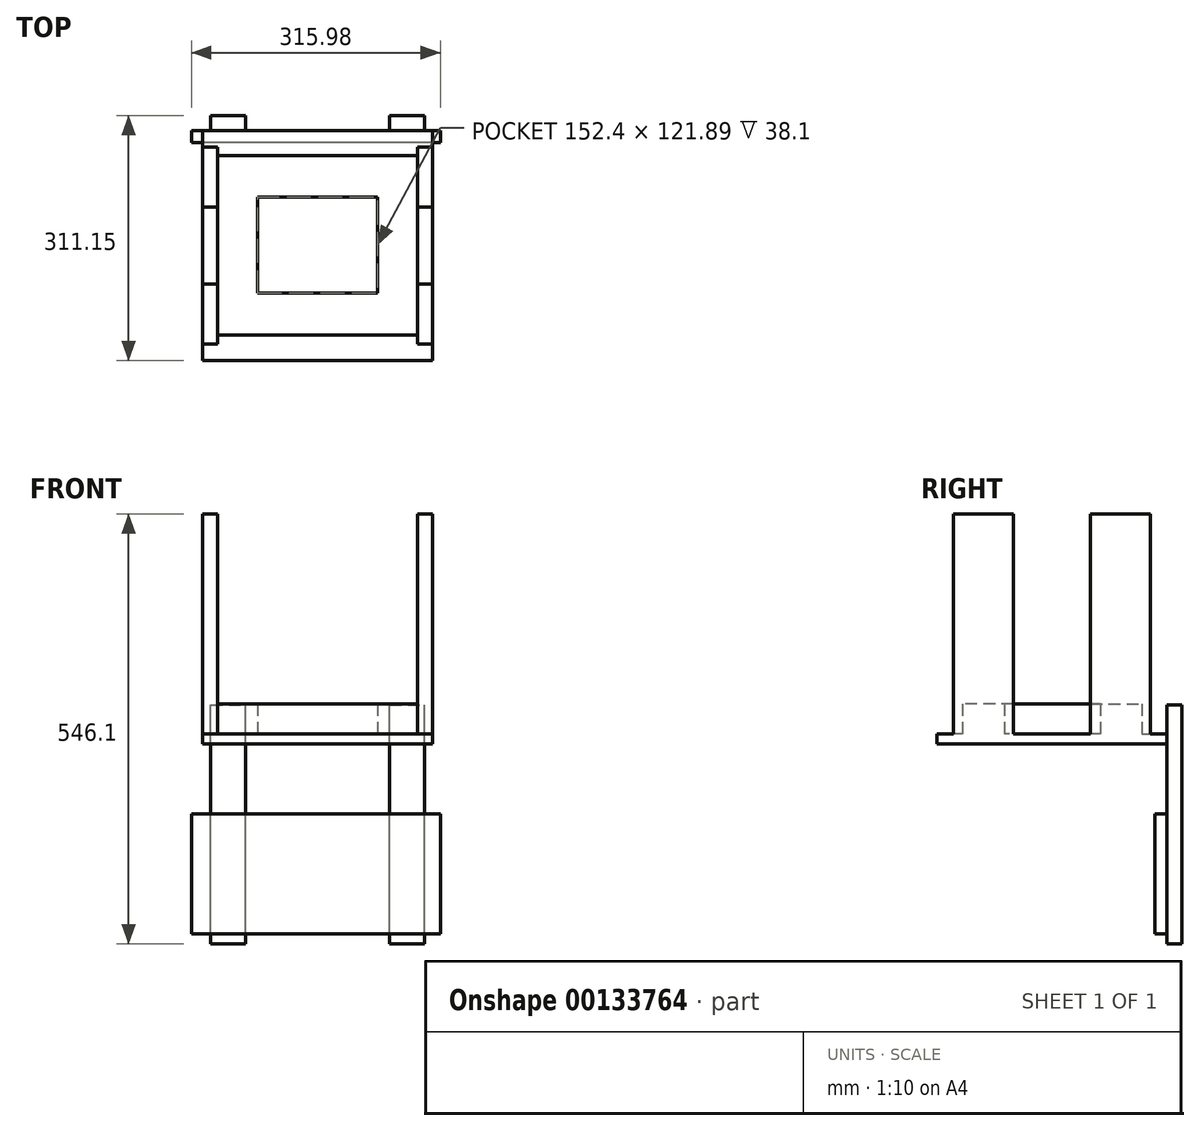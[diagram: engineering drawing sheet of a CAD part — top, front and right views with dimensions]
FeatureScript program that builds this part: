
annotation { "Feature Type Name" : "Feature", "Feature Type Description" : "" }
export const myFeature = defineFeature(function(context is Context, id is Id, definition is map)
    precondition{}
    {
        {
            var Q0;
            Q0=qCreatedBy(makeId("Top.planeOp"),FACE);
            var sketch = newSketch(context, id + "F0", { "sketchPlane" : qUnion([Q0])});
            skLineSegment(sketch, "E0.bottom", {"start": v(-155.55, 178.7) * mm, "end": v(136.55, 178.7) * mm});
            skLineSegment(sketch, "E0.top", {"start": v(-155.55, -113.4) * mm, "end": v(136.55, -113.4) * mm});
            skLineSegment(sketch, "E0.left", {"start": v(-155.55, 178.7) * mm, "end": v(-155.55, -113.4) * mm});
            skLineSegment(sketch, "E0.right", {"start": v(136.55, 178.7) * mm, "end": v(136.55, -113.4) * mm});
            skSolve(sketch);
        }
        {
            var Q0;
            Q0=makeQuery(id+"F0.imprint","IMPRINT",FACE,{"disambiguationData":[TD([[makeQuery(id+"F0.imprint","IMPRINT",EDGE,{"derivedFrom":sQuery(id+"F0.wireOp",EDGE,"E0.bottom")}),-1.0]])]});
            extrude(context, id + "F1", {"entities" : qUnion([Q0]), "oppositeDirection" : true, "depth" : 12.7 * mm});
        }
        {
            var Q0;
            Q0=makeQuery(id+"F1.opExtrude","CAP_FACE",FACE,{"disambiguationData":[OSD([sQuery(id+"F0.wireOp",EDGE,"E0.bottom"),sQuery(id+"F0.wireOp",EDGE,"E0.top"),sQuery(id+"F0.wireOp",EDGE,"E0.left"),sQuery(id+"F0.wireOp",EDGE,"E0.right")])],"isStart":false});
            var sketch = newSketch(context, id + "F2", { "sketchPlane" : qUnion([Q0])});
            skLineSegment(sketch, "E1.bottom", {"start": v(-136.5, 94.34) * mm, "end": v(117.5, 94.34) * mm});
            skLineSegment(sketch, "E1.top", {"start": v(-136.5, -159.66) * mm, "end": v(117.5, -159.66) * mm});
            skLineSegment(sketch, "E1.left", {"start": v(-136.5, 94.34) * mm, "end": v(-136.5, -159.66) * mm});
            skLineSegment(sketch, "E1.right", {"start": v(117.5, 94.34) * mm, "end": v(117.5, -159.66) * mm});
            skLineSegment(sketch, "E2.bottom", {"start": v(-111.1, 68.94) * mm, "end": v(92.1, 68.94) * mm});
            skLineSegment(sketch, "E2.top", {"start": v(-111.1, -134.26) * mm, "end": v(92.1, -134.26) * mm});
            skLineSegment(sketch, "E2.left", {"start": v(-111.1, 68.94) * mm, "end": v(-111.1, -134.26) * mm});
            skLineSegment(sketch, "E2.right", {"start": v(92.1, 68.94) * mm, "end": v(92.1, -134.26) * mm});
            skLineSegment(sketch, "E3", {"start": v(-9.5, 307.78) * mm, "end": v(-9.5, -178.7) * mm, "construction": true});
            skSolve(sketch);
        }
        {
            var Q0;
            Q0=makeQuery(id+"F1.opExtrude","CAP_FACE",FACE,{"disambiguationData":[OSD([sQuery(id+"F0.wireOp",EDGE,"E0.bottom"),sQuery(id+"F0.wireOp",EDGE,"E0.top"),sQuery(id+"F0.wireOp",EDGE,"E0.left"),sQuery(id+"F0.wireOp",EDGE,"E0.right")])],"isStart":true});
            var sketch = newSketch(context, id + "F3", { "sketchPlane" : qUnion([Q0])});
            skLineSegment(sketch, "E4.bottom", {"start": v(-155.55, -16.34) * mm, "end": v(-136.5, -16.34) * mm});
            skLineSegment(sketch, "E4.top", {"start": v(-155.55, -92.54) * mm, "end": v(-136.5, -92.54) * mm});
            skLineSegment(sketch, "E4.left", {"start": v(-155.55, -16.34) * mm, "end": v(-155.55, -92.54) * mm});
            skLineSegment(sketch, "E4.right", {"start": v(-136.5, -16.34) * mm, "end": v(-136.5, -92.54) * mm});
            skLineSegment(sketch, "E5.MirrorCS", {"start": v(117.5, -16.34) * mm, "end": v(117.5, -92.54) * mm});
            skLineSegment(sketch, "E6.MirrorCS", {"start": v(136.55, -16.34) * mm, "end": v(136.55, -92.54) * mm});
            skLineSegment(sketch, "E7.MirrorCS", {"start": v(136.55, -92.54) * mm, "end": v(117.5, -92.54) * mm});
            skLineSegment(sketch, "E8.MirrorCS", {"start": v(136.55, -16.34) * mm, "end": v(117.5, -16.34) * mm});
            skLineSegment(sketch, "E9", {"start": v(-155.55, 32.66) * mm, "end": v(136.55, 32.66) * mm, "construction": true});
            skLineSegment(sketch, "E10.MirrorCS", {"start": v(-155.55, 81.66) * mm, "end": v(-155.55, 157.86) * mm});
            skLineSegment(sketch, "E11.MirrorCS", {"start": v(-136.5, 81.66) * mm, "end": v(-136.5, 157.86) * mm});
            skLineSegment(sketch, "E12.MirrorCS", {"start": v(-155.55, 157.86) * mm, "end": v(-136.5, 157.86) * mm});
            skLineSegment(sketch, "E13.MirrorCS", {"start": v(-155.55, 81.66) * mm, "end": v(-136.5, 81.66) * mm});
            skLineSegment(sketch, "E14.MirrorCS", {"start": v(117.5, 81.66) * mm, "end": v(117.5, 157.86) * mm});
            skLineSegment(sketch, "E15.MirrorCS", {"start": v(136.55, 81.66) * mm, "end": v(117.5, 81.66) * mm});
            skLineSegment(sketch, "E16.MirrorCS", {"start": v(136.55, 157.86) * mm, "end": v(117.5, 157.86) * mm});
            skLineSegment(sketch, "E17.MirrorCS", {"start": v(136.55, 81.66) * mm, "end": v(136.55, 157.86) * mm});
            skSolve(sketch);
        }
        {
            var Q0;
            Q0=makeQuery(id+"F3.imprint","IMPRINT",FACE,{"disambiguationData":[TD([[makeQuery(id+"F3.imprint","IMPRINT",EDGE,{"derivedFrom":sQuery(id+"F3.wireOp",EDGE,"E6.MirrorCS")}),-1.0]])]});
            var Q1;
            Q1=makeQuery(id+"F3.imprint","IMPRINT",FACE,{"disambiguationData":[TD([[makeQuery(id+"F3.imprint","IMPRINT",EDGE,{"derivedFrom":sQuery(id+"F3.wireOp",EDGE,"E14.MirrorCS")}),-1.0]])]});
            var Q2;
            Q2=makeQuery(id+"F3.imprint","IMPRINT",FACE,{"disambiguationData":[TD([[makeQuery(id+"F3.imprint","IMPRINT",EDGE,{"derivedFrom":sQuery(id+"F3.wireOp",EDGE,"E4.bottom")}),-1.0]])]});
            var Q3;
            Q3=makeQuery(id+"F3.imprint","IMPRINT",FACE,{"disambiguationData":[TD([[makeQuery(id+"F3.imprint","IMPRINT",EDGE,{"derivedFrom":sQuery(id+"F3.wireOp",EDGE,"E10.MirrorCS")}),1.0]])]});
            extrude(context, id + "F4", {"entities" : qUnion([Q0, Q1, Q2, Q3]), "operationType" : NewBodyOperationType.ADD, "depth" : 279.4 * mm});
        }
        {
            var Q0;
            Q0=makeQuery(id+"F4.opExtrude","SWEPT_FACE",FACE,{"disambiguationData":[OSD([sQuery(id+"F3.wireOp",EDGE,"E5.MirrorCS")])]});
            var sketch = newSketch(context, id + "F5", { "sketchPlane" : qUnion([Q0])});
            skSolve(sketch);
        }
        {
            var Q0;
            {var subQ0=sQuery(id+"F3.wireOp",EDGE,"E5.MirrorCS");Q0=makeQuery(id+"F5.imprint","IMPRINT",FACE,{"disambiguationData":[TD([[makeQuery(id+"F5.imprint","IMPRINT",EDGE,{"derivedFrom":makeQuery(id+"F4.opExtrude","CAP_EDGE",EDGE,{"disambiguationData":[OSD([subQ0])],"isStart":false})}),-1.0]])]});}
            var sketch = newSketch(context, id + "F6", { "sketchPlane" : qUnion([Q0])});
            skLineSegment(sketch, "E18.bottom", {"start": v(80.96, 0) * mm, "end": v(27.92, 0) * mm});
            skLineSegment(sketch, "E18.top", {"start": v(80.96, 38.1) * mm, "end": v(27.92, 38.1) * mm});
            skLineSegment(sketch, "E18.left", {"start": v(80.96, 0) * mm, "end": v(80.96, 38.1) * mm});
            skLineSegment(sketch, "E18.right", {"start": v(27.92, 0) * mm, "end": v(27.92, 38.1) * mm});
            skLineSegment(sketch, "E19", {"start": v(-33.02, -13.3) * mm, "end": v(-33.02, 292.13) * mm});
            skLineSegment(sketch, "E20.MirrorCS", {"start": v(-147, 0) * mm, "end": v(-147, 38.1) * mm});
            skLineSegment(sketch, "E21.MirrorCS", {"start": v(-147, 0) * mm, "end": v(-93.97, 0) * mm});
            skLineSegment(sketch, "E22.MirrorCS", {"start": v(-147, 38.1) * mm, "end": v(-93.97, 38.1) * mm});
            skLineSegment(sketch, "E23.MirrorCS", {"start": v(-93.97, 0) * mm, "end": v(-93.97, 38.1) * mm});
            skSolve(sketch);
        }
        {
            var Q0;
            Q0=makeQuery(id+"F6.imprint","IMPRINT",FACE,{"disambiguationData":[TD([[makeQuery(id+"F6.imprint","IMPRINT",EDGE,{"derivedFrom":sQuery(id+"F6.wireOp",EDGE,"E18.bottom")}),1.0]])]});
            var Q1;
            Q1=makeQuery(id+"F6.imprint","IMPRINT",FACE,{"disambiguationData":[TD([[makeQuery(id+"F6.imprint","IMPRINT",EDGE,{"derivedFrom":sQuery(id+"F6.wireOp",EDGE,"E20.MirrorCS")}),-1.0]])]});
            var Q2;
            Q2=makeQuery(id+"F4.opExtrude","SWEPT_FACE",FACE,{"disambiguationData":[OSD([sQuery(id+"F3.wireOp",EDGE,"E4.right")])]});
            extrude(context, id + "F7", {"entities" : qUnion([Q0, Q1]), "operationType" : NewBodyOperationType.ADD, "endBound" : BoundingType.UP_TO_SURFACE, "endBoundEntityFace" : qUnion([Q2]), "depth" : 25.4 * mm});
        }
        {
            var Q0;
            Q0=makeQuery(id+"F4.boolean.opBoolean","MERGE",FACE,{"derivedFrom":[makeQuery(id+"F1.opExtrude","SWEPT_FACE",FACE,{"disambiguationData":[OSD([sQuery(id+"F0.wireOp",EDGE,"E0.right")])]}),makeQuery(id+"F4.opExtrude","SWEPT_FACE",FACE,{"disambiguationData":[OSD([sQuery(id+"F3.wireOp",EDGE,"E6.MirrorCS")])]}),makeQuery(id+"F4.opExtrude","SWEPT_FACE",FACE,{"disambiguationData":[OSD([sQuery(id+"F3.wireOp",EDGE,"E17.MirrorCS")])]})]});
            var Q1;
            Q1=makeQuery(id+"F4.boolean.opBoolean","MERGE",FACE,{"derivedFrom":[makeQuery(id+"F1.opExtrude","SWEPT_FACE",FACE,{"disambiguationData":[OSD([sQuery(id+"F0.wireOp",EDGE,"E0.left")])]}),makeQuery(id+"F4.opExtrude","SWEPT_FACE",FACE,{"disambiguationData":[OSD([sQuery(id+"F3.wireOp",EDGE,"E4.left")])]}),makeQuery(id+"F4.opExtrude","SWEPT_FACE",FACE,{"disambiguationData":[OSD([sQuery(id+"F3.wireOp",EDGE,"E10.MirrorCS")])]})]});
            cPlane(context, id + "F8", {"entities" : qUnion([Q0, Q1]), "cplaneType" : CPlaneType.MID_PLANE, "offset" : 25.4 * mm, "width" : 152.4 * mm, "height" : 152.4 * mm});
        }
        {
            var Q0;
            Q0=makeQuery(id+"F7.opExtrude","SWEPT_FACE",FACE,{"disambiguationData":[OSD([sQuery(id+"F6.wireOp",EDGE,"E18.right")])]});
            var sketch = newSketch(context, id + "F9", { "sketchPlane" : qUnion([Q0])});
            skLineSegment(sketch, "E24", {"start": v(-66.7, 38.1) * mm, "end": v(-66.7, 0) * mm});
            skLineSegment(sketch, "E25.0", {"start": v(136.5, 0) * mm, "end": v(-117.5, 0) * mm});
            skLineSegment(sketch, "E26", {"start": v(9.5, 0) * mm, "end": v(9.5, 123.46) * mm, "construction": true});
            skLineSegment(sketch, "E27.MirrorCS", {"start": v(9.5, -25.4) * mm, "end": v(9.5, -148.86) * mm, "construction": true});
            skLineSegment(sketch, "E28.MirrorCS", {"start": v(85.7, 38.1) * mm, "end": v(85.7, 0) * mm});
            skSolve(sketch);
        }
        {
            var Q0;
            {var subQ0=sQuery(id+"F9.wireOp",EDGE,"E24");Q0=makeQuery(id+"F9.imprint","IMPRINT",FACE,{"disambiguationData":[TD([[makeQuery(id+"F9.imprint","IMPRINT",EDGE,{"derivedFrom":subQ0}),-1.0]])]});}
            var Q1;
            {var subQ3=sQuery(id+"F9.wireOp",EDGE,"E28.MirrorCS");Q1=makeQuery(id+"F9.imprint","IMPRINT",FACE,{"disambiguationData":[TD([[makeQuery(id+"F9.imprint","IMPRINT",EDGE,{"derivedFrom":subQ3}),1.0]])]});}
            var Q2;
            Q2=makeQuery(id+"F7.opExtrude","SWEPT_FACE",FACE,{"disambiguationData":[OSD([sQuery(id+"F6.wireOp",EDGE,"E23.MirrorCS")])]});
            extrude(context, id + "F10", {"entities" : qUnion([Q0, Q1]), "operationType" : NewBodyOperationType.ADD, "endBound" : BoundingType.UP_TO_SURFACE, "endBoundEntityFace" : qUnion([Q2]), "depth" : 25.4 * mm});
        }
        {
            var Q0;
            Q0=makeQuery(id+"F1.opExtrude","CAP_FACE",FACE,{"disambiguationData":[OSD([sQuery(id+"F0.wireOp",EDGE,"E0.bottom"),sQuery(id+"F0.wireOp",EDGE,"E0.top"),sQuery(id+"F0.wireOp",EDGE,"E0.left"),sQuery(id+"F0.wireOp",EDGE,"E0.right")])],"isStart":false});
            var sketch = newSketch(context, id + "F11", { "sketchPlane" : qUnion([Q0])});
            skLineSegment(sketch, "E29.0", {"start": v(-155.55, -178.7) * mm, "end": v(136.55, -178.7) * mm, "construction": true});
            skLineSegment(sketch, "E30", {"start": v(-9.5, -257.44) * mm, "end": v(-9.5, 125.73) * mm, "construction": true});
            skPoint(sketch, "E30.startSnap0", {"position": v(-9.5, -178.7) * mm});
            skLineSegment(sketch, "E31.bottom", {"start": v(126.39, -178.7) * mm, "end": v(81.94, -178.7) * mm});
            skLineSegment(sketch, "E31.top", {"start": v(126.39, -197.76) * mm, "end": v(81.94, -197.76) * mm});
            skLineSegment(sketch, "E31.left", {"start": v(126.39, -178.7) * mm, "end": v(126.39, -197.76) * mm});
            skLineSegment(sketch, "E31.right", {"start": v(81.94, -178.7) * mm, "end": v(81.94, -197.76) * mm});
            skLineSegment(sketch, "E32.MirrorCS", {"start": v(-145.4, -197.76) * mm, "end": v(-100.94, -197.76) * mm});
            skLineSegment(sketch, "E33.MirrorCS", {"start": v(-145.4, -178.7) * mm, "end": v(-100.94, -178.7) * mm});
            skLineSegment(sketch, "E34.MirrorCS", {"start": v(-100.94, -178.7) * mm, "end": v(-100.94, -197.76) * mm});
            skLineSegment(sketch, "E35.MirrorCS", {"start": v(-145.4, -178.7) * mm, "end": v(-145.4, -197.76) * mm});
            skSolve(sketch);
        }
        {
            var Q0;
            Q0=makeQuery(id+"F11.imprint","IMPRINT",FACE,{"disambiguationData":[TD([[makeQuery(id+"F11.imprint","IMPRINT",EDGE,{"derivedFrom":sQuery(id+"F11.wireOp",EDGE,"E31.bottom")}),-1.0]])]});
            var Q1;
            Q1=makeQuery(id+"F11.imprint","IMPRINT",FACE,{"disambiguationData":[TD([[makeQuery(id+"F11.imprint","IMPRINT",EDGE,{"derivedFrom":sQuery(id+"F11.wireOp",EDGE,"E32.MirrorCS")}),1.0]])]});
            extrude(context, id + "F12", {"entities" : qUnion([Q0, Q1]), "operationType" : NewBodyOperationType.ADD, "depth" : 254 * mm, "hasSecondDirection" : true, "secondDirectionOppositeDirection" : true, "secondDirectionDepth" : 49.9 * mm});
        }
        {
            var Q0;
            {var subQ2=sQuery(id+"F11.wireOp",EDGE,"E31.bottom");var subQ3=sQuery(id+"F0.wireOp",EDGE,"E0.bottom");Q0=makeQuery(id+"F12.boolean.opBoolean","SPLIT",FACE,{"disambiguationData":[TD([makeQuery(id+"F1.opExtrude","CAP_FACE",FACE,{"disambiguationData":[OSD([subQ3,sQuery(id+"F0.wireOp",EDGE,"E0.top"),sQuery(id+"F0.wireOp",EDGE,"E0.left"),sQuery(id+"F0.wireOp",EDGE,"E0.right")])],"isStart":false})])],"derivedFrom":makeQuery(id+"F12.opExtrude","SWEPT_FACE",FACE,{"disambiguationData":[OSD([subQ2])]})});}
            var sketch = newSketch(context, id + "F13", { "sketchPlane" : qUnion([Q0])});
            skLineSegment(sketch, "E36.bottom", {"start": v(146.19, -254) * mm, "end": v(-169.8, -254) * mm});
            skLineSegment(sketch, "E36.top", {"start": v(146.19, -101.6) * mm, "end": v(-169.8, -101.6) * mm});
            skLineSegment(sketch, "E36.left", {"start": v(146.19, -254) * mm, "end": v(146.19, -101.6) * mm});
            skLineSegment(sketch, "E36.right", {"start": v(-169.8, -254) * mm, "end": v(-169.8, -101.6) * mm});
            skSolve(sketch);
        }
        {
            var Q0;
            {var subQ0=sQuery(id+"F13.wireOp",EDGE,"E36.left");Q0=makeQuery(id+"F13.imprint","IMPRINT",FACE,{"disambiguationData":[TD([[makeQuery(id+"F13.imprint","IMPRINT",EDGE,{"derivedFrom":subQ0}),1.0]])]});}
            var Q1;
            {var subQ0=sQuery(id+"F13.wireOp",EDGE,"E36.bottom");var subQ1=sQuery(id+"F11.wireOp",EDGE,"E31.right");var subQ2=sQuery(id+"F11.wireOp",EDGE,"E31.left");var subQ3=sQuery(id+"F11.wireOp",EDGE,"E31.bottom");var subQ4=makeQuery(id+"F12.opExtrude","CAP_FACE",FACE,{"disambiguationData":[OSD([subQ3,sQuery(id+"F11.wireOp",EDGE,"E31.top"),subQ2,subQ1])],"isStart":false});var subQ5=makeQuery(id+"F12.opExtrude","SWEPT_FACE",FACE,{"disambiguationData":[OSD([subQ3])]});var subQ6=sQuery(id+"F0.wireOp",EDGE,"E0.bottom");var subQ7=makeQuery(id+"F1.opExtrude","CAP_FACE",FACE,{"disambiguationData":[OSD([subQ6,sQuery(id+"F0.wireOp",EDGE,"E0.top"),sQuery(id+"F0.wireOp",EDGE,"E0.left"),sQuery(id+"F0.wireOp",EDGE,"E0.right")])],"isStart":false});var subQ8=makeQuery(id+"F1.opExtrude","SWEPT_FACE",FACE,{"disambiguationData":[OSD([subQ6])]});var subQ9=makeQuery(id+"F12.boolean.opBoolean","SPLIT",EDGE,{"disambiguationData":[TD([subQ8,subQ7,subQ5,subQ4,makeQuery(id+"F12.opExtrude","SWEPT_FACE",FACE,{"disambiguationData":[OSD([subQ2])]})])],"derivedFrom":makeQuery(id+"F12.opExtrude","SWEPT_EDGE",EDGE,{"disambiguationData":[OSD([subQ6,subQ3,subQ2])]})});var subQ10=makeQuery(id+"F13.imprint","INTERSECT",VERTEX,{"derivedFrom":[subQ9,subQ0]});Q1=makeQuery(id+"F13.imprint","IMPRINT",FACE,{"disambiguationData":[TD([[makeQuery(id+"F13.imprint","IMPRINT",EDGE,{"disambiguationData":[TD([[subQ10,-1.0]])],"derivedFrom":subQ0}),-1.0]])]});}
            var Q2;
            {var subQ0=sQuery(id+"F13.wireOp",EDGE,"E36.right");Q2=makeQuery(id+"F13.imprint","IMPRINT",FACE,{"disambiguationData":[TD([[makeQuery(id+"F13.imprint","IMPRINT",EDGE,{"derivedFrom":subQ0}),-1.0]])]});}
            extrude(context, id + "F14", {"entities" : qUnion([Q0, Q1, Q2]), "operationType" : NewBodyOperationType.ADD, "depth" : 15.24 * mm});
        }
    });
